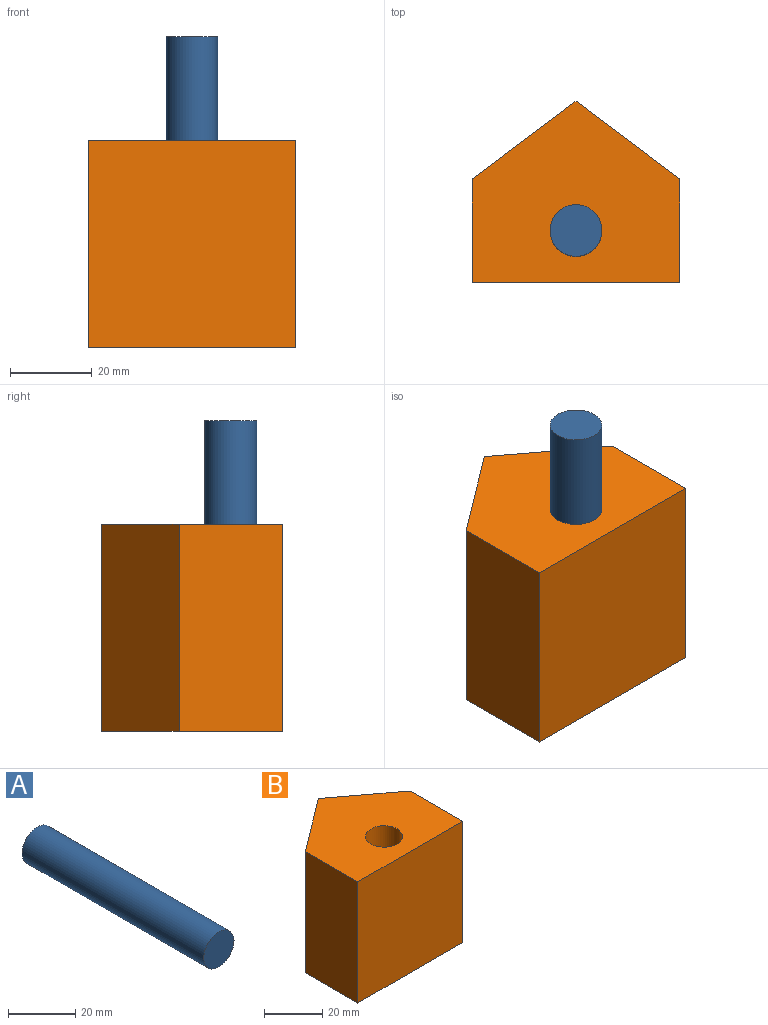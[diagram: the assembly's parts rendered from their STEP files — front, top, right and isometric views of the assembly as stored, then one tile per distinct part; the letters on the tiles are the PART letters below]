
ASSEMBLY  parts=2 mates=1
PART A: 3 faces, bbox 12.7x76.2x12.7 mm
  f0: plane 12.7x12.7mm, normal (0,1,0), area 126.7mm2, adj f2
  f1: plane 12.7x12.7mm, normal (0,-1,0), area 126.7mm2, adj f2
  f2: cylinder r=6.35mm len=76.2mm, axis (0,-1,0), area 3040.2mm2, adj f0,f1
PART B: 8 faces, bbox 50.8x44.5x50.8 mm
  f0: plane 50.8x25.4mm, normal (1,0,0), area 1290.3mm2, adj f1,f4,f5,f6
  f1: plane 50.8x25.4mm, normal (0.6,0.8,0), area 1612.9mm2, adj f0,f2,f5,f6
  f2: plane 50.8x25.4mm, normal (-0.6,0.8,0), area 1612.9mm2, adj f1,f3,f5,f6
  f3: plane 50.8x25.4mm, normal (-1,0,0), area 1290.3mm2, adj f2,f4,f5,f6
  f4: plane 50.8x50.8mm, normal (0,-1,0), area 2580.6mm2, adj f0,f3,f5,f6
  f5: plane 50.8x44.45mm, normal (0,0,1), area 1647.5mm2, adj f0,f1,f2,f3,f4,f7
  f6: plane 50.8x44.45mm, normal (0,0,-1), area 1647.5mm2, adj f0,f1,f2,f3,f4,f7
  f7: cylinder r=6.35mm len=50.8mm, axis (0,0,-1), area 2026.8mm2, adj f5,f6
PLACE A rot(axis=(-1,0,0),90deg) t=(0.03,-0.28,50.8)mm
PLACE B t=(-25.37,-12.98,-25.4)mm fixed
MATE revolute B.f7 <-> A.f2  axis (0,0,1) through (0.03,-0.28,25.4)mm
